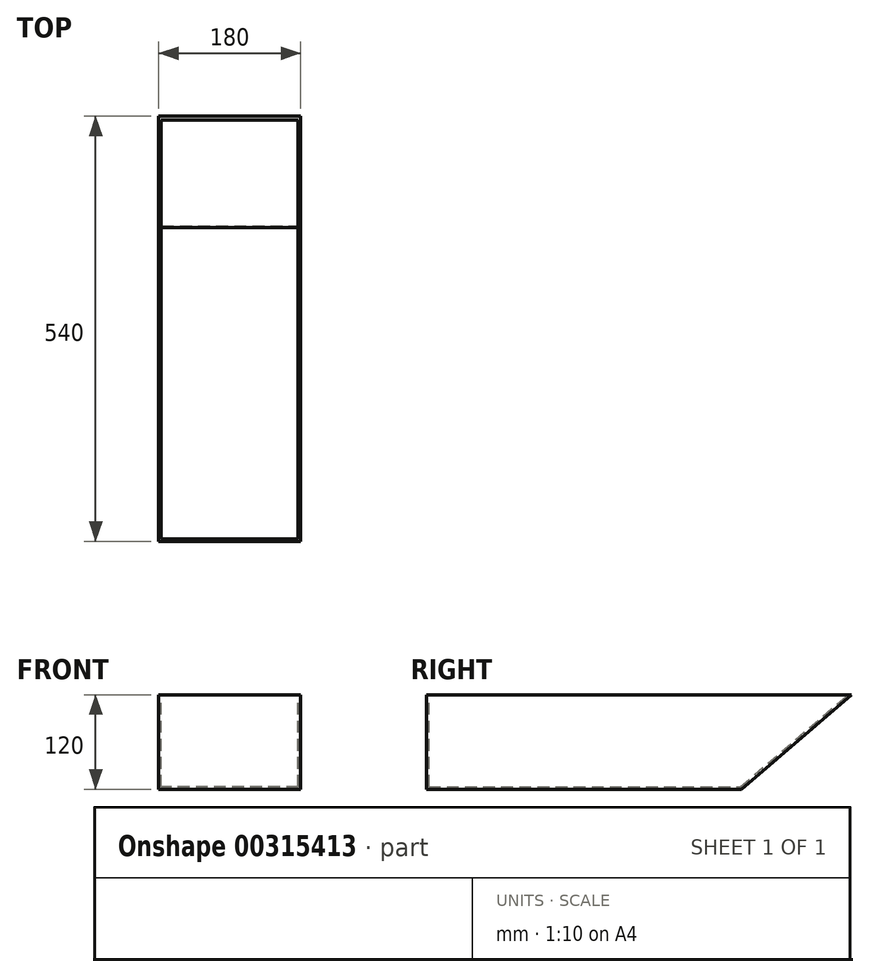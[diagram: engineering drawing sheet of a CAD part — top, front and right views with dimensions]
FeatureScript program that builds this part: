
annotation { "Feature Type Name" : "Feature", "Feature Type Description" : "" }
export const myFeature = defineFeature(function(context is Context, id is Id, definition is map)
    precondition{}
    {
        {
            var Q0;
            Q0=qCreatedBy(makeId("Right.planeOp"),FACE);
            var sketch = newSketch(context, id + "F0", { "sketchPlane" : qUnion([Q0])});
            skLineSegment(sketch, "E0.bottom", {"start": v(-200, -60) * mm, "end": v(200, -60) * mm});
            skLineSegment(sketch, "E0.top", {"start": v(-200, 60) * mm, "end": v(200, 60) * mm});
            skLineSegment(sketch, "E0.left", {"start": v(-200, -60) * mm, "end": v(-200, 60) * mm});
            skPoint(sketch, "E0.middle", {"position": v(0, 0) * mm});
            skLineSegment(sketch, "E1", {"start": v(200, -60) * mm, "end": v(340, 60) * mm});
            skLineSegment(sketch, "E2", {"start": v(340, 60) * mm, "end": v(200, 60) * mm});
            skSolve(sketch);
        }
        {
            var Q0;
            Q0=qSketchRegion(id+"F0",true);
            extrude(context, id + "F1", {"entities" : qUnion([Q0]), "depth" : 180 * mm});
        }
        {
            var Q0;
            Q0=makeQuery(id+"F1.opExtrude","SWEPT_FACE",FACE,{"disambiguationData":[OSD([sQuery(id+"F0.wireOp",EDGE,"E0.top"),sQuery(id+"F0.wireOp",EDGE,"E2")])]});
            shell(context, id + "F2", {"entities" : qUnion([Q0]), "thickness" : 3 * mm});
        }
    });
